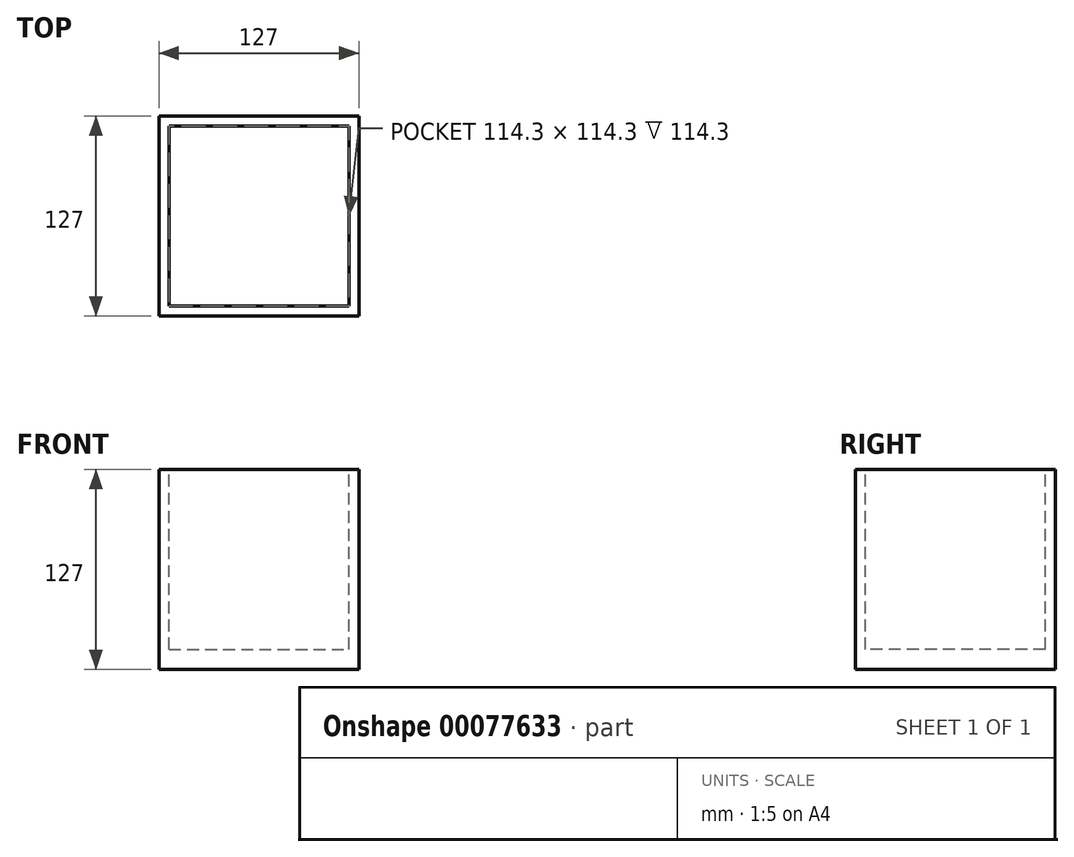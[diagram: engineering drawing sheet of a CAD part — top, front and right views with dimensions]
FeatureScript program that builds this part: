
annotation { "Feature Type Name" : "Feature", "Feature Type Description" : "" }
export const myFeature = defineFeature(function(context is Context, id is Id, definition is map)
    precondition{}
    {
        {
            var Q0;
            Q0=qCreatedBy(makeId("Front.planeOp"),FACE);
            var sketch = newSketch(context, id + "F0", { "sketchPlane" : qUnion([Q0])});
            skLineSegment(sketch, "E0", {"start": v(0, 0) * mm, "end": v(0, 127) * mm});
            skLineSegment(sketch, "E1", {"start": v(0, 127) * mm, "end": v(127, 127) * mm});
            skLineSegment(sketch, "E2", {"start": v(127, 127) * mm, "end": v(127, 0) * mm});
            skLineSegment(sketch, "E3", {"start": v(127, 0) * mm, "end": v(0, 0) * mm});
            skSolve(sketch);
        }
        {
            var Q0;
            Q0 = qSketchRegion(id + "F0", true);
            extrude(context, id + "F1", {"entities" : qUnion([Q0]), "depth" : 127 * mm});
        }
        {
            var Q0;
            Q0=makeQuery(id+"F1.opExtrude","SWEPT_FACE",FACE,{"disambiguationData":[OSD([sQuery(id+"F0.wireOp",EDGE,"E1")])]});
            var sketch = newSketch(context, id + "F2", { "sketchPlane" : qUnion([Q0])});
            skLineSegment(sketch, "E4.bottom", {"start": v(6.35, -6.35) * mm, "end": v(120.65, -6.35) * mm});
            skLineSegment(sketch, "E4.top", {"start": v(6.35, -120.65) * mm, "end": v(120.65, -120.65) * mm});
            skLineSegment(sketch, "E4.left", {"start": v(6.35, -6.35) * mm, "end": v(6.35, -120.65) * mm});
            skLineSegment(sketch, "E4.right", {"start": v(120.65, -6.35) * mm, "end": v(120.65, -120.65) * mm});
            skSolve(sketch);
        }
        {
            var Q0;
            Q0=makeQuery(id+"F2.imprint","IMPRINT",FACE,{"disambiguationData":[TD([[makeQuery(id+"F2.imprint","IMPRINT",EDGE,{"derivedFrom":sQuery(id+"F2.wireOp",EDGE,"E4.bottom")}),-1.0]])]});
            extrude(context, id + "F3", {"entities" : qUnion([Q0]), "operationType" : NewBodyOperationType.REMOVE, "oppositeDirection" : true, "depth" : 114.3 * mm});
        }
    });
